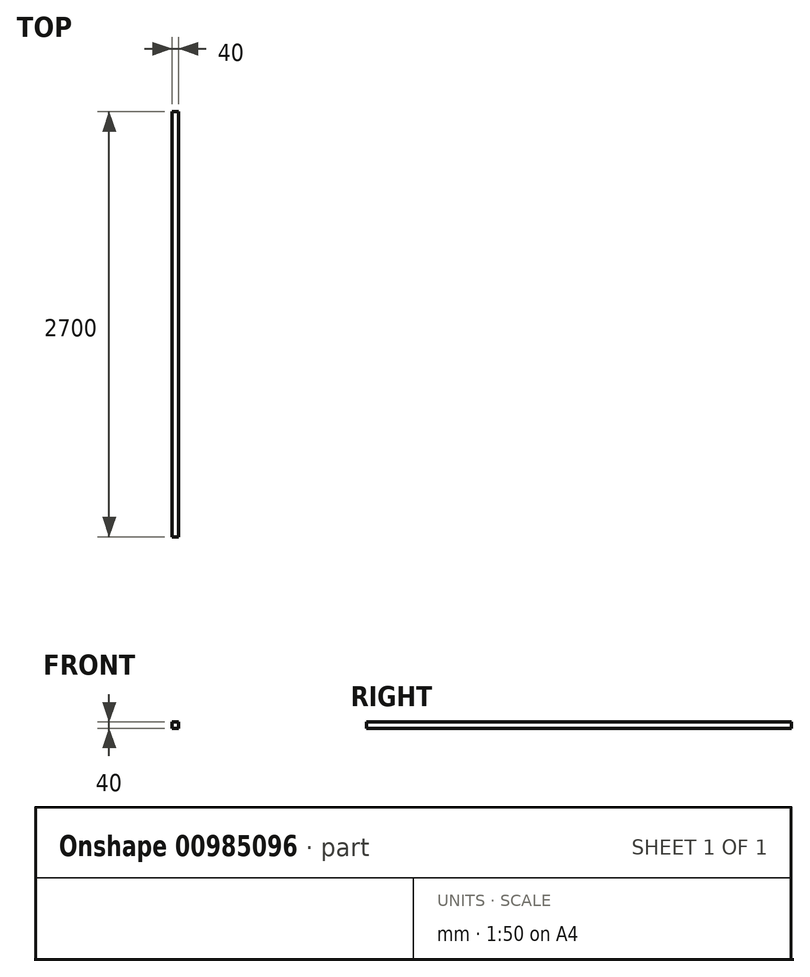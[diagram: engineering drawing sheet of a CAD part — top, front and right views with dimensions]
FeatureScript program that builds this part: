
annotation { "Feature Type Name" : "Feature", "Feature Type Description" : "" }
export const myFeature = defineFeature(function(context is Context, id is Id, definition is map)
    precondition{}
    {
        {
            var Q0;
            Q0=qCreatedBy(makeId("Front.planeOp"),FACE);
            var sketch = newSketch(context, id + "F0", { "sketchPlane" : qUnion([Q0])});
            skLineSegment(sketch, "E0.bottom", {"start": v(20, -20) * mm, "end": v(-20, -20) * mm});
            skLineSegment(sketch, "E0.top", {"start": v(20, 20) * mm, "end": v(-20, 20) * mm});
            skLineSegment(sketch, "E0.left", {"start": v(20, -20) * mm, "end": v(20, 20) * mm});
            skLineSegment(sketch, "E0.right", {"start": v(-20, -20) * mm, "end": v(-20, 20) * mm});
            skPoint(sketch, "E0.middle", {"position": v(0, 0) * mm});
            skSolve(sketch);
        }
        {
            var Q0;
            Q0 = qSketchRegion(id + "F0", true);
            extrude(context, id + "F1", {"entities" : qUnion([Q0]), "depth" : 2700 * mm, "offsetDistance" : 25 * mm});
        }
    });
